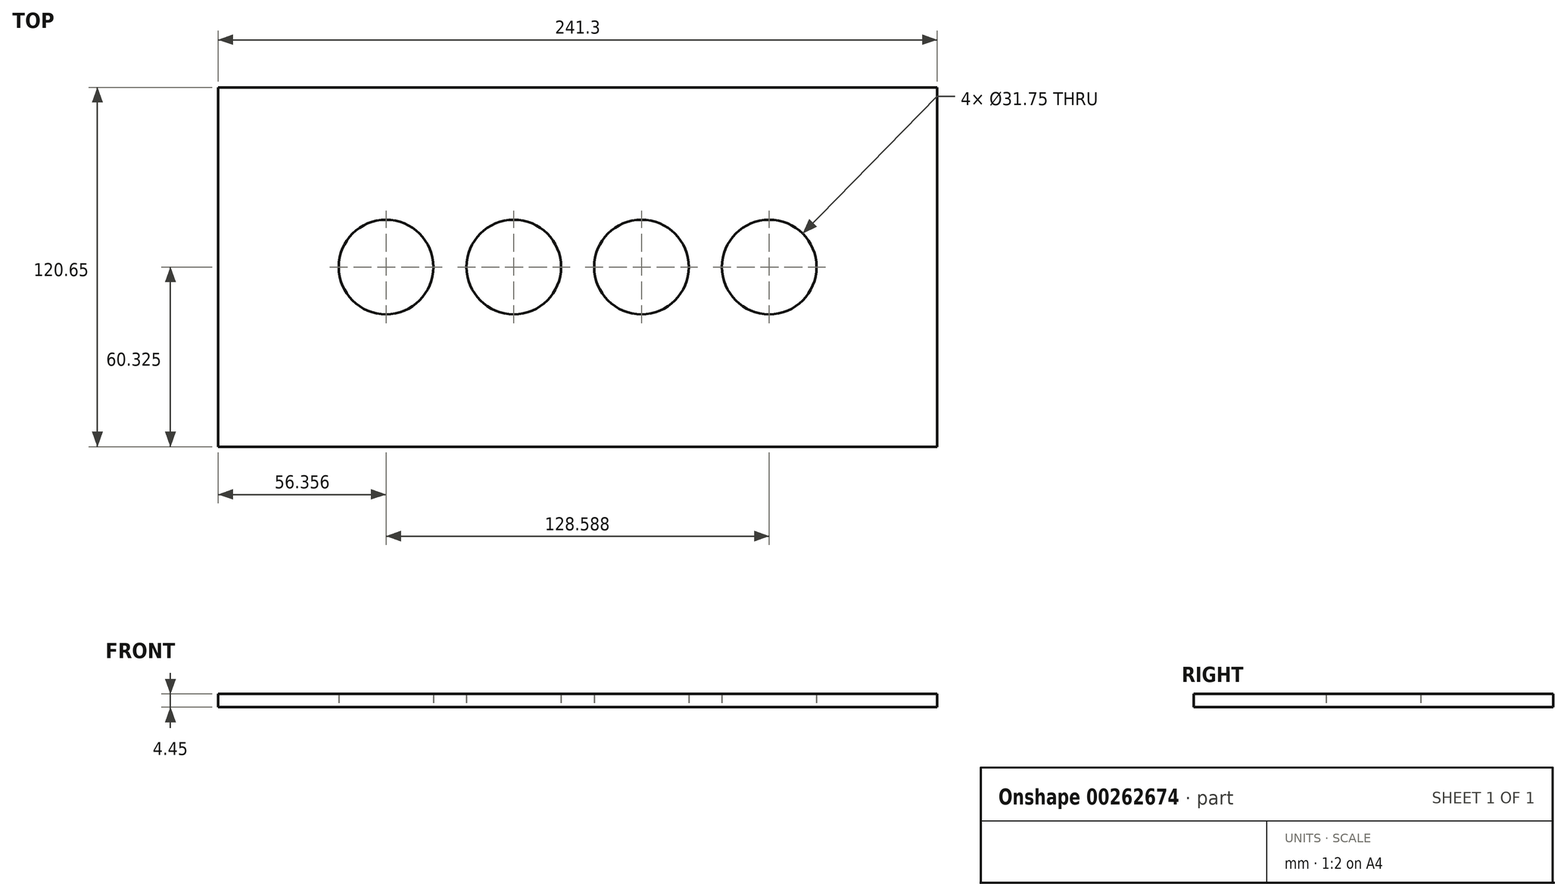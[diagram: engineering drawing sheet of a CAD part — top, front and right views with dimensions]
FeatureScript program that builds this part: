
annotation { "Feature Type Name" : "Feature", "Feature Type Description" : "" }
export const myFeature = defineFeature(function(context is Context, id is Id, definition is map)
    precondition{}
    {
        {
            var Q0;
            Q0=qCreatedBy(makeId("Top.planeOp"),FACE);
            var sketch = newSketch(context, id + "F0", { "sketchPlane" : qUnion([Q0])});
            skLineSegment(sketch, "E0.bottom", {"start": v(0, 0) * mm, "end": v(241.3, 0) * mm});
            skLineSegment(sketch, "E0.top", {"start": v(0, 120.65) * mm, "end": v(241.3, 120.65) * mm});
            skLineSegment(sketch, "E0.left", {"start": v(0, 0) * mm, "end": v(0, 120.65) * mm});
            skLineSegment(sketch, "E0.right", {"start": v(241.3, 0) * mm, "end": v(241.3, 120.65) * mm});
            skCircle(sketch, "E1", {"center": v(56.36, 60.33) * mm, "radius": 15.88 * mm});
            skPoint(sketch, "E1.centerSnap0", {"position": v(0, 60.33) * mm});
            skCircle(sketch, "E2", {"center": v(99.22, 60.33) * mm, "radius": 15.88 * mm});
            skCircle(sketch, "E3", {"center": v(142.08, 60.33) * mm, "radius": 15.88 * mm});
            skCircle(sketch, "E4", {"center": v(184.94, 60.33) * mm, "radius": 15.88 * mm});
            skSolve(sketch);
        }
        {
            var Q0;
            Q0=makeQuery(id+"F0.imprint","IMPRINT",FACE,{"disambiguationData":[TD([[makeQuery(id+"F0.imprint","IMPRINT",EDGE,{"derivedFrom":sQuery(id+"F0.wireOp",EDGE,"E0.bottom")}),1.0]])]});
            extrude(context, id + "F1", {"entities" : qUnion([Q0]), "depth" : 4.44 * mm});
        }
    });
